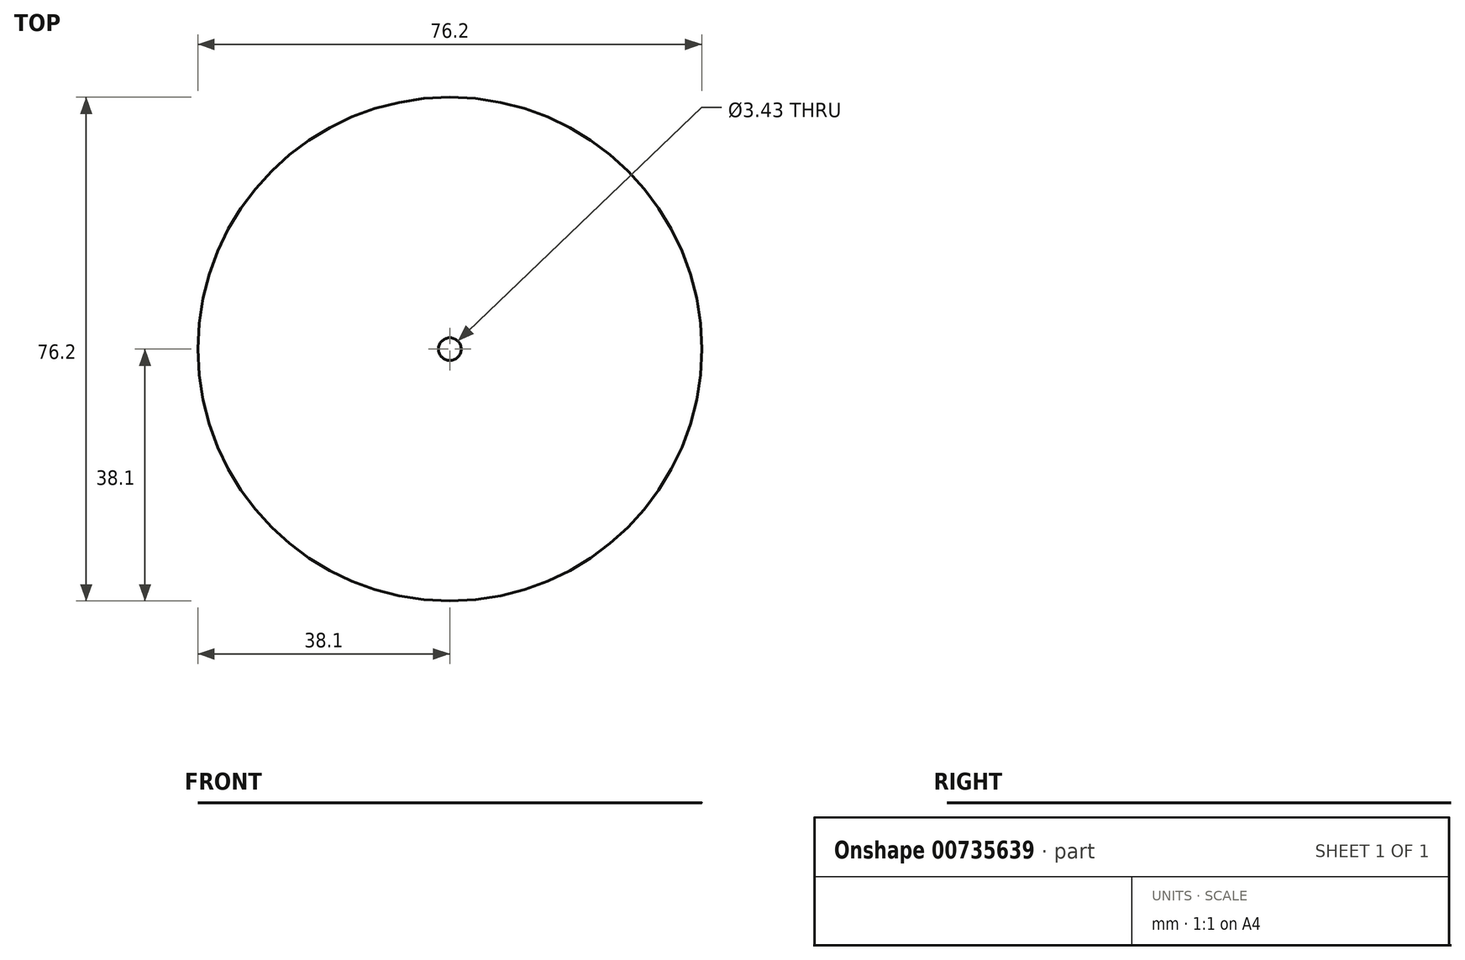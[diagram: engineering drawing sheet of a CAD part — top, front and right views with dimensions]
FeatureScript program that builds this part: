
annotation { "Feature Type Name" : "Feature", "Feature Type Description" : "" }
export const myFeature = defineFeature(function(context is Context, id is Id, definition is map)
    precondition{}
    {
        {
            var Q0;
            Q0=qCreatedBy(makeId("Top.planeOp"),FACE);
            var sketch = newSketch(context, id + "F0", { "sketchPlane" : qUnion([Q0])});
            skCircle(sketch, "E0", {"center": v(0, 0) * mm, "radius": 38.1 * mm});
            skSolve(sketch);
        }
        {
            var Q0;
            Q0 = qSketchRegion(id + "F0", true);
            extrude(context, id + "F1", {"entities" : qUnion([Q0]), "depth" : 1 / 203.2 * mm, "offsetDistance" : 25.4 * mm});
        }
        {
            var Q0;
            Q0=makeQuery(id+"F1.opExtrude","CAP_FACE",FACE,{"disambiguationData":[OSD([sQuery(id+"F0.wireOp",EDGE,"E0")])],"isStart":false});
            var sketch = newSketch(context, id + "F2", { "sketchPlane" : qUnion([Q0])});
            skCircle(sketch, "E1", {"center": v(0, 0) * mm, "radius": 1.71 * mm});
            skSolve(sketch);
        }
        {
            var Q0;
            Q0 = qSketchRegion(id + "F2", true);
            extrude(context, id + "F3", {"entities" : qUnion([Q0]), "operationType" : NewBodyOperationType.REMOVE, "endBound" : BoundingType.THROUGH_ALL, "oppositeDirection" : true, "depth" : 25.4 * mm, "offsetDistance" : 25.4 * mm});
        }
    });
